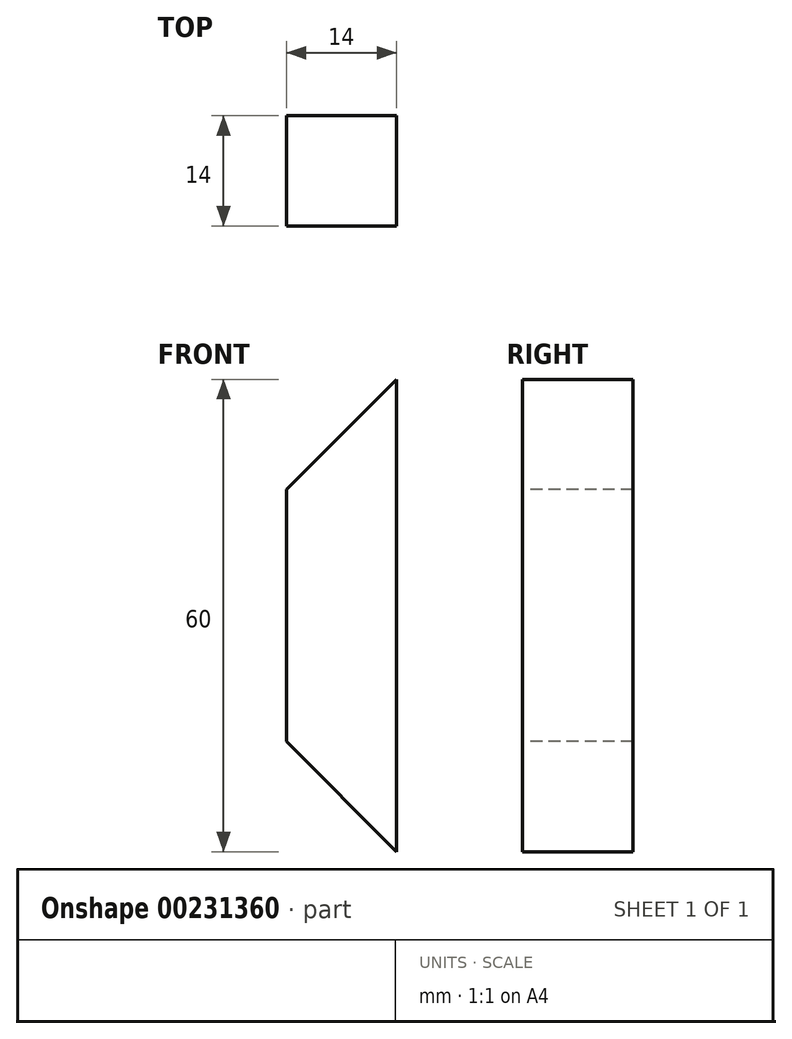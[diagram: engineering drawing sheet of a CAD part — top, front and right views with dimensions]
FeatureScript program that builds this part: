
annotation { "Feature Type Name" : "Feature", "Feature Type Description" : "" }
export const myFeature = defineFeature(function(context is Context, id is Id, definition is map)
    precondition{}
    {
        {
            var Q0;
            Q0=qCreatedBy(makeId("Top.planeOp"),FACE);
            var sketch = newSketch(context, id + "F0", { "sketchPlane" : qUnion([Q0])});
            skLineSegment(sketch, "E0.bottom", {"start": v(7, -7) * mm, "end": v(-7, -7) * mm});
            skLineSegment(sketch, "E0.top", {"start": v(7, 7) * mm, "end": v(-7, 7) * mm});
            skLineSegment(sketch, "E0.left", {"start": v(7, -7) * mm, "end": v(7, 7) * mm});
            skLineSegment(sketch, "E0.right", {"start": v(-7, -7) * mm, "end": v(-7, 7) * mm});
            skPoint(sketch, "E0.middle", {"position": v(0, 0) * mm});
            skSolve(sketch);
        }
        {
            var Q0;
            Q0=qSketchRegion(id+"F0",true);
            extrude(context, id + "F1", {"entities" : qUnion([Q0]), "depth" : 60 * mm});
        }
        {
            var Q0;
            Q0=makeQuery(id+"F1.opExtrude","SWEPT_FACE",FACE,{"disambiguationData":[OSD([sQuery(id+"F0.wireOp",EDGE,"E0.bottom")])]});
            var sketch = newSketch(context, id + "F2", { "sketchPlane" : qUnion([Q0])});
            skLineSegment(sketch, "E1", {"start": v(7, 60) * mm, "end": v(-7, 46) * mm});
            skLineSegment(sketch, "E2", {"start": v(-7, 46) * mm, "end": v(-7, 60) * mm});
            skLineSegment(sketch, "E3", {"start": v(-7, 60) * mm, "end": v(7, 60) * mm});
            skSolve(sketch);
        }
        {
            var Q0;
            Q0=qSketchRegion(id+"F2",true);
            extrude(context, id + "F3", {"entities" : qUnion([Q0]), "operationType" : NewBodyOperationType.REMOVE, "oppositeDirection" : true, "depth" : 25 * mm});
        }
        {
            var Q0;
            Q0=makeQuery(id+"F1.opExtrude","SWEPT_FACE",FACE,{"disambiguationData":[OSD([sQuery(id+"F0.wireOp",EDGE,"E0.bottom")])]});
            var sketch = newSketch(context, id + "F4", { "sketchPlane" : qUnion([Q0])});
            skLineSegment(sketch, "E4", {"start": v(7, 0) * mm, "end": v(-7, 14) * mm});
            skLineSegment(sketch, "E5", {"start": v(-7, 14) * mm, "end": v(-7, 0) * mm});
            skLineSegment(sketch, "E6", {"start": v(-7, 0) * mm, "end": v(7, 0) * mm});
            skSolve(sketch);
        }
        {
            var Q0;
            Q0 = qSketchRegion(id + "F4", true);
            extrude(context, id + "F5", {"entities" : qUnion([Q0]), "operationType" : NewBodyOperationType.REMOVE, "oppositeDirection" : true, "depth" : 25 * mm});
        }
    });
